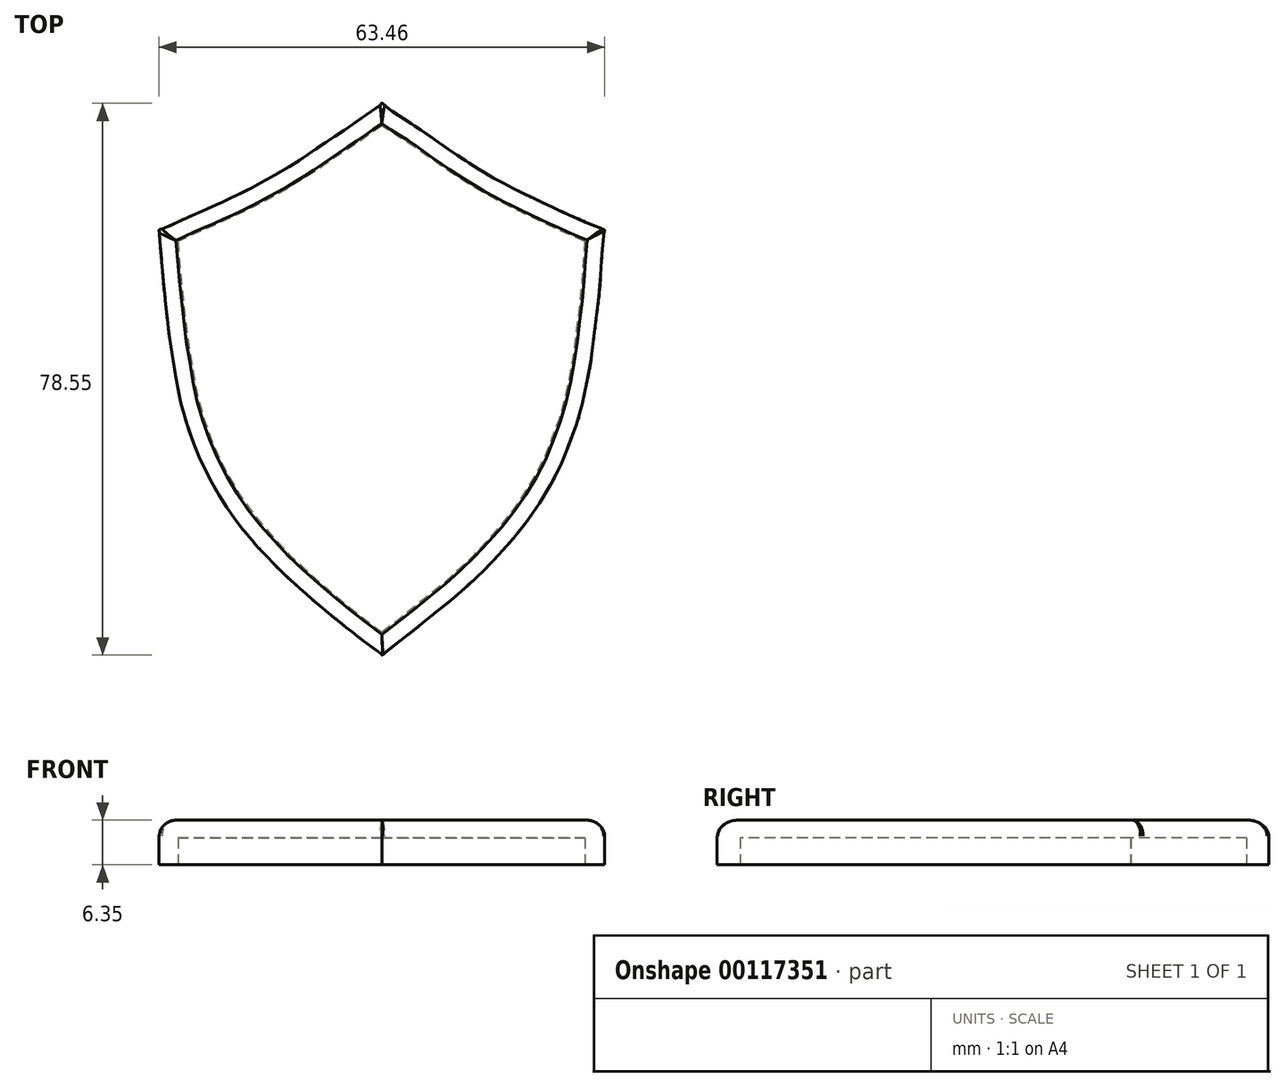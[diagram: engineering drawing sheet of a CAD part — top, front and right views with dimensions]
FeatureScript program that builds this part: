
annotation { "Feature Type Name" : "Feature", "Feature Type Description" : "" }
export const myFeature = defineFeature(function(context is Context, id is Id, definition is map)
    precondition{}
    {
        {
            var Q0;
            Q0=qCreatedBy(makeId("Top.planeOp"),FACE);
            var sketch = newSketch(context, id + "F0", { "sketchPlane" : qUnion([Q0])});
            skFitSpline(sketch, "E0", {"points": [v(-18.42, -22.98) * mm, v(-18.09, -23.42) * mm, v(-17.6, -23.94) * mm, v(-17.17, -24.36) * mm, v(-16.58, -25.01) * mm, v(-15.77, -25.84) * mm, v(-14.92, -26.76) * mm, v(-10.58, -30.73) * mm, v(-9.46, -31.7) * mm, v(-7.03, -33.72) * mm, v(-1.32, -38.17) * mm, v(0, -39.2) * mm, v(0, -39.24) * mm, v(1.07, -38.37) * mm, v(2, -37.66) * mm, v(2.98, -36.9) * mm, v(5.17, -35.17) * mm, v(8.53, -32.45) * mm, v(9.2, -31.95) * mm, v(14.77, -26.92) * mm, v(16.78, -24.76) * mm, v(17.69, -23.8) * mm, v(18.5, -22.86) * mm, v(19.22, -22) * mm, v(20.63, -20.2) * mm, v(21.24, -19.35) * mm, v(23.27, -16.27) * mm, v(24.45, -14.2) * mm, v(26.09, -10.76) * mm, v(26.29, -10.17) * mm, v(27.1, -7.91) * mm, v(28.15, -4.96) * mm, v(29, -1.16) * mm, v(29.68, 2.21) * mm, v(30.23, 6.57) * mm, v(30.93, 12.23) * mm, v(31.2, 15.89) * mm, v(31.67, 21.08) * mm, v(31.72, 21.22) * mm, v(29.58, 22.14) * mm, v(21.94, 25.62) * mm, v(17.33, 27.9) * mm, v(13.6, 30.05) * mm, v(9.45, 32.8) * mm, v(4.55, 36.18) * mm, v(0.52, 38.9) * mm, v(0, 39.31) * mm, v(-0.29, 39.04) * mm, v(-1.69, 38.06) * mm, v(-4.73, 35.93) * mm, v(-8.34, 33.52) * mm, v(-10.25, 32.2) * mm, v(-14.04, 29.8) * mm, v(-17.79, 27.68) * mm, v(-22.9, 25.18) * mm, v(-26.88, 23.41) * mm, v(-29.56, 22.2) * mm, v(-31.3, 21.43) * mm, v(-31.7, 21.31) * mm, v(-31.7, 20.96) * mm, v(-31.63, 20.18) * mm, v(-31.16, 14.38) * mm, v(-30.73, 10.25) * mm, v(-30.32, 6.65) * mm, v(-29.77, 3) * mm, v(-29.15, -0.79) * mm, v(-28.6, -3.43) * mm, v(-27.3, -7.71) * mm, v(-25.6, -11.92) * mm, v(-23.66, -15.68) * mm, v(-21.55, -18.98) * mm, v(-19.66, -21.5) * mm, v(-18.42, -22.98) * mm]});
            skSolve(sketch);
        }
        {
            var Q0;
            Q0 = qSketchRegion(id + "F0", true);
            extrude(context, id + "F1", {"entities" : qUnion([Q0]), "depth" : 6.35 * mm});
        }
        {
            var Q0;
            Q0=makeQuery(id+"F1.opExtrude","CAP_EDGE",EDGE,{"disambiguationData":[OSD([sQuery(id+"F0.wireOp",EDGE,"E0")])],"isStart":false});
            fillet(context, id + "F2", {"entities" : qUnion([Q0]), "radius" : 2.3 * mm, "tangentPropagation" : true, "allowEdgeOverflow" : false});
        }
        {
            var Q0;
            Q0=makeQuery(id+"F1.opExtrude","CAP_FACE",FACE,{"disambiguationData":[OSD([sQuery(id+"F0.wireOp",EDGE,"E0")])],"isStart":true});
            shell(context, id + "F3", {"entities" : qUnion([Q0]), "thickness" : 2.54 * mm});
        }
    });
